# Revit family: Window_Sliding_Flush_Ready-Access_275LP
name_source: partatom
category: Windows
units: mm (PartAtom-declared; Revit-internal decimal feet)

## family parameters
Always vertical = Yes
Classification Number = 23.30.20.24.14
Cut with Voids When Loaded = No
Host = Wall
Room Calculation Point = No
Shared = No

## types (6) — shared parameters
Air Infiltration = as Specified
Assembly Code = B2020100
Construction Details = http://www.arcat.com
Electrical_Amperage = 0 A
Electrical_Frequency = 0 Hz
Electrical_Voltage = 0 V
Forced Entry Rating = as Specified
Frame Thickness = 0' - 4"
Keynote = 08582
Manufacturer = Ready Access
Manufacturer Fax = 630-876-7767
Manufacturer Website = http://www.ready-access.com
Meets Egress = as Specified
Miami Dade Conformance = as Specified
Product Data = http://www.arcat.com
Sales Information = http://www.ready-access.com
Send Message = http://www.arcat.com
Specification = http://www.arcat.com
Standards Conformance = as Specified
Structural Test Pressure = as Specified
URL = http://www.ready-access.com
Wall Closure = By host
Water Penetration = as Specified
zero-valued in all types: Expected Lifespan (Years), Maintenance Schedule (Months), Sound Transmission Class (STC), Warranty Duration (Years)

## per-type parameters (varying)
| type | Description | Fixed Window Width | Height | Model | Service Opening Height | Service Opening Width | Width |
| MOER 19x39 Serving Area | Ready Access MOER Sliding Service Window - 275LPMOER as Specified | 1' - 11 1/4" | 3' - 7 1/2" | 275LPMOER | 3' - 3" | 1' - 7" | 3' - 11 1/2" |
| MOER 19x32 Serving Area | Ready Access MOER Sliding Service Window - 275LPMOER as Specified | 1' - 11 1/4" | 2' - 11 3/4" | 275LPMOER | 2' - 8" | 1' - 7" | 3' - 11 1/2" |
| MOER 14x32 Serving Area | Ready Access MOER Sliding Service Window - 275LPMOER as Specified | 1' - 5" | 2' - 11 3/4" | 275LPMOER | 2' - 8" | 1' - 2" | 2' - 11 3/4" |
| Manual Self Closing 19x39 Serving Area | Ready Access Manual Self Closing Sliding Service Window - 275LPSC as Specified | 1' - 11 1/4" | 3' - 7 1/2" | 275LPSC | 3' - 3" | 1' - 7" | 3' - 11 1/2" |
| Manual Self Closing 19x32 Serving Area | Ready Access Manual Self Closing Sliding Service Window - 275LPSC as Specified | 1' - 11 1/4" | 2' - 11 3/4" | 275LPSC | 2' - 8" | 1' - 7" | 3' - 11 1/2" |
| Manual Self Closing 14x32 Serving Area | Ready Access Manual Self Closing Sliding Service Window - 275LPSC as Specified | 1' - 5" | 2' - 11 3/4" | 275LPSC | 2' - 8" | 1' - 2" | 2' - 11 3/4" |

## geometry (parser evidence)
native form markers: Sweep x3
no freeform markers — native parametric forms only
